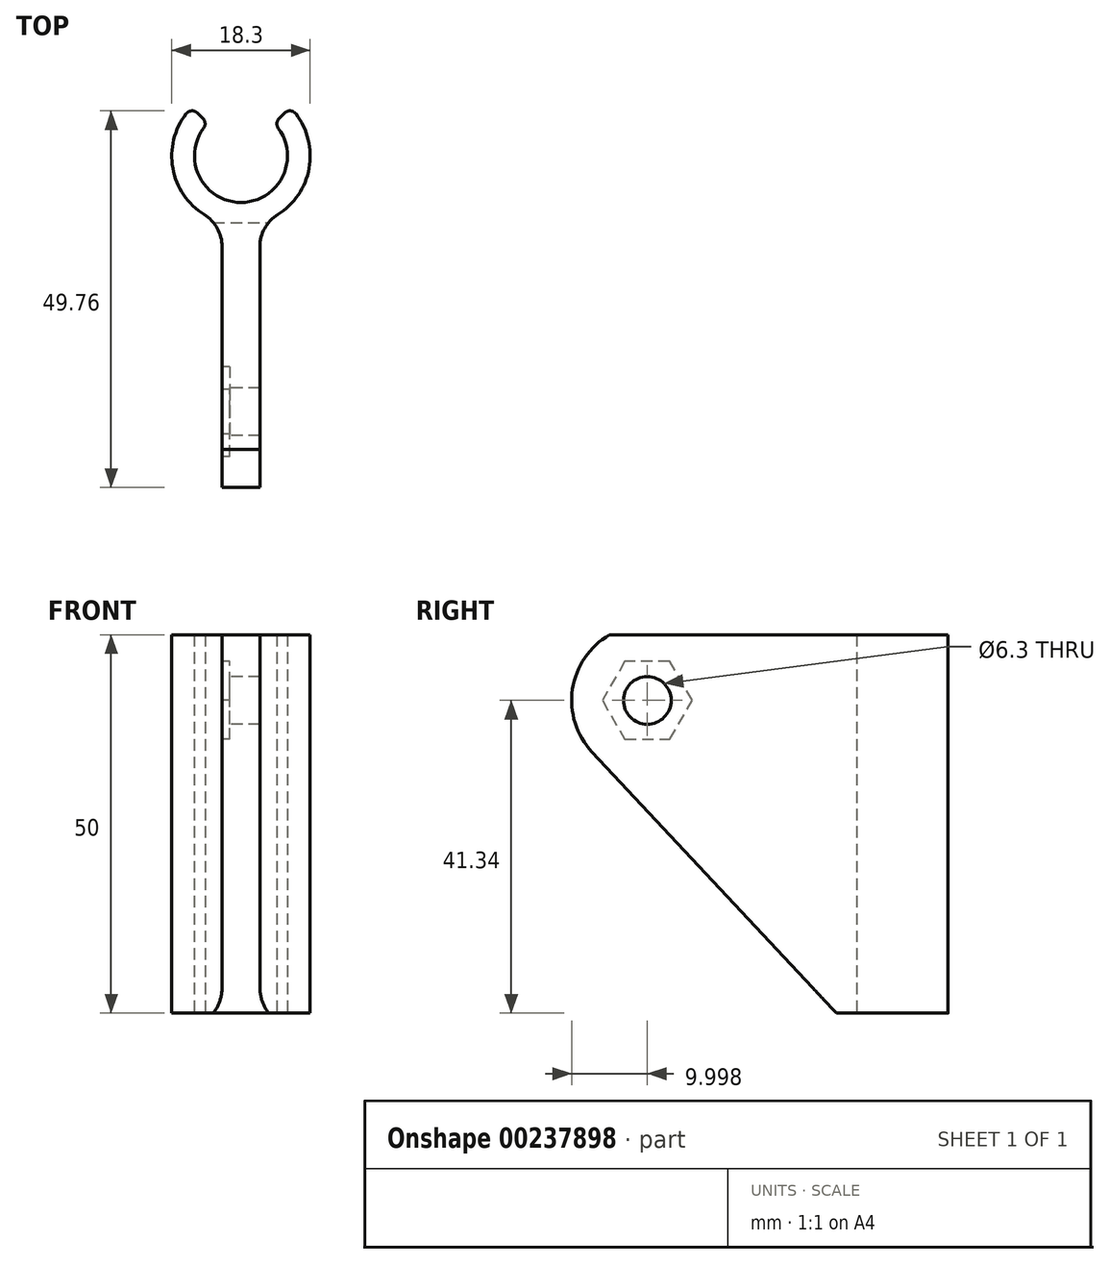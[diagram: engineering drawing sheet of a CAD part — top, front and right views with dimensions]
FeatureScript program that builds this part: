
annotation { "Feature Type Name" : "Feature", "Feature Type Description" : "" }
export const myFeature = defineFeature(function(context is Context, id is Id, definition is map)
    precondition{}
    {
        {
            var Q0;
            Q0=qCreatedBy(makeId("Top.planeOp"),FACE);
            var sketch = newSketch(context, id + "F0", { "sketchPlane" : qUnion([Q0])});
            skArc(sketch, "E0", {"start": v(-4.95, 3.66) * mm, "mid": v(0, -6.15) * mm, "end": v(4.95, 3.66) * mm});
            skArc(sketch, "E1", {"start": v(2.5, -8.8) * mm, "mid": v(8.69, -2.88) * mm, "end": v(7.26, 5.56) * mm});
            skLineSegment(sketch, "E2", {"start": v(-2.5, -8.8) * mm, "end": v(2.5, -8.8) * mm});
            skLineSegment(sketch, "E3", {"start": v(-5.05, 4.96) * mm, "end": v(-5.77, 5.67) * mm});
            skLineSegment(sketch, "E4", {"start": v(5.05, 4.96) * mm, "end": v(5.77, 5.67) * mm});
            skArc(sketch, "E5.trimOffspring", {"start": v(-7.26, 5.56) * mm, "mid": v(-8.69, -2.88) * mm, "end": v(-2.5, -8.8) * mm});
            skPoint(sketch, "E6.visualSharp", {"position": v(-4.39, 4.31) * mm});
            skArc(sketch, "E6.filletArc", {"start": v(-4.95, 3.66) * mm, "mid": v(-4.75, 4.33) * mm, "end": v(-5.05, 4.96) * mm});
            skPoint(sketch, "E7.visualSharp", {"position": v(-6.53, 6.41) * mm});
            skArc(sketch, "E7.filletArc", {"start": v(-5.77, 5.67) * mm, "mid": v(-6.54, 5.95) * mm, "end": v(-7.26, 5.56) * mm});
            skPoint(sketch, "E8.visualSharp", {"position": v(4.39, 4.31) * mm});
            skArc(sketch, "E8.filletArc", {"start": v(5.05, 4.96) * mm, "mid": v(4.75, 4.33) * mm, "end": v(4.95, 3.66) * mm});
            skPoint(sketch, "E9.visualSharp", {"position": v(6.53, 6.41) * mm});
            skArc(sketch, "E9.filletArc", {"start": v(7.26, 5.56) * mm, "mid": v(6.54, 5.95) * mm, "end": v(5.77, 5.67) * mm});
            skSolve(sketch);
        }
        {
            var Q0;
            Q0=makeQuery(id+"F0.imprint","IMPRINT",FACE,{"disambiguationData":[TD([[makeQuery(id+"F0.imprint","IMPRINT",EDGE,{"derivedFrom":sQuery(id+"F0.wireOp",EDGE,"E0")}),-1.0]])]});
            extrude(context, id + "F1", {"entities" : qUnion([Q0]), "depth" : 50 * mm});
        }
        {
            var Q0;
            Q0=qCreatedBy(makeId("Right.planeOp"),FACE);
            var sketch = newSketch(context, id + "F2", { "sketchPlane" : qUnion([Q0])});
            skLineSegment(sketch, "E10", {"start": v(-8.8, 0) * mm, "end": v(-8.8, 50) * mm});
            skLineSegment(sketch, "E11", {"start": v(-8.8, 50) * mm, "end": v(-38.8, 50) * mm});
            skLineSegment(sketch, "E12", {"start": v(-41.1, 34.5) * mm, "end": v(-8.8, 0) * mm});
            skPoint(sketch, "E13.visualSharp", {"position": v(-55.6, 50) * mm});
            skArc(sketch, "E13.filletArc", {"start": v(-38.8, 50) * mm, "mid": v(-43.7, 42.8) * mm, "end": v(-41.1, 34.5) * mm});
            skLineSegment(sketch, "E14", {"start": v(-38.8, 50) * mm, "end": v(-57.65, 39.12) * mm, "construction": true});
            skCircle(sketch, "E15", {"center": v(-33.8, 41.34) * mm, "radius": 3.15 * mm});
            skSolve(sketch);
        }
        {
            var Q0;
            Q0=makeQuery(id+"F2.imprint","IMPRINT",FACE,{"disambiguationData":[TD([[makeQuery(id+"F2.imprint","IMPRINT",EDGE,{"derivedFrom":sQuery(id+"F2.wireOp",EDGE,"E10")}),1.0]])]});
            extrude(context, id + "F3", {"entities" : qUnion([Q0]), "operationType" : NewBodyOperationType.ADD, "depth" : 5 * mm, "symmetric" : true});
        }
        {
            var Q0;
            Q0=makeQuery(id+"F3.opExtrude","CAP_FACE",FACE,{"disambiguationData":[OSD([sQuery(id+"F2.wireOp",EDGE,"E10"),sQuery(id+"F2.wireOp",EDGE,"E11"),sQuery(id+"F2.wireOp",EDGE,"E12"),sQuery(id+"F2.wireOp",EDGE,"E13.filletArc"),sQuery(id+"F2.wireOp",EDGE,"E15")])],"isStart":true});
            var sketch = newSketch(context, id + "F4", { "sketchPlane" : qUnion([Q0])});
            skCircle(sketch, "E16.cCircle", {"center": v(33.8, 41.34) * mm, "radius": 5.15 * mm, "construction": true});
            skLineSegment(sketch, "E16.0", {"start": v(30.83, 46.49) * mm, "end": v(36.78, 46.49) * mm});
            skLineSegment(sketch, "E16.1", {"start": v(36.78, 46.49) * mm, "end": v(39.75, 41.34) * mm});
            skLineSegment(sketch, "E16.2", {"start": v(39.75, 41.34) * mm, "end": v(36.78, 36.19) * mm});
            skLineSegment(sketch, "E16.3", {"start": v(36.78, 36.19) * mm, "end": v(30.83, 36.19) * mm});
            skLineSegment(sketch, "E16.4", {"start": v(30.83, 36.19) * mm, "end": v(27.86, 41.34) * mm});
            skLineSegment(sketch, "E16.5", {"start": v(27.86, 41.34) * mm, "end": v(30.83, 46.49) * mm});
            skPoint(sketch, "E16.0.midPoint", {"position": v(33.8, 46.49) * mm});
            skSolve(sketch);
        }
        {
            var Q0;
            Q0=makeQuery(id+"F4.imprint","IMPRINT",FACE,{"disambiguationData":[TD([[makeQuery(id+"F4.imprint","IMPRINT",EDGE,{"derivedFrom":sQuery(id+"F4.wireOp",EDGE,"E16.0")}),-1.0]])]});
            extrude(context, id + "F5", {"entities" : qUnion([Q0]), "operationType" : NewBodyOperationType.REMOVE, "oppositeDirection" : true, "depth" : 1 * mm});
        }
        {
            var Q0;
            Q0=makeQuery(id+"F3.boolean.opBoolean","MERGE",EDGE,{"derivedFrom":[makeQuery(id+"F1.opExtrude","SWEPT_EDGE",EDGE,{"disambiguationData":[OSD([sQuery(id+"F0.wireOp",EDGE,"E1"),sQuery(id+"F0.wireOp",EDGE,"E2")])]}),makeQuery(id+"F3.opExtrude","CAP_EDGE",EDGE,{"disambiguationData":[OSD([sQuery(id+"F2.wireOp",EDGE,"E10")])],"isStart":false})]});
            var Q1;
            Q1=makeQuery(id+"F3.boolean.opBoolean","MERGE",EDGE,{"derivedFrom":[makeQuery(id+"F1.opExtrude","SWEPT_EDGE",EDGE,{"disambiguationData":[OSD([sQuery(id+"F0.wireOp",EDGE,"E2"),sQuery(id+"F0.wireOp",EDGE,"E5.trimOffspring")])]}),makeQuery(id+"F3.opExtrude","CAP_EDGE",EDGE,{"disambiguationData":[OSD([sQuery(id+"F2.wireOp",EDGE,"E10")])],"isStart":true})]});
            fillet(context, id + "F6", {"entities" : qUnion([Q0, Q1]), "radius" : 5 * mm, "tangentPropagation" : true, "allowEdgeOverflow" : false});
        }
    });
